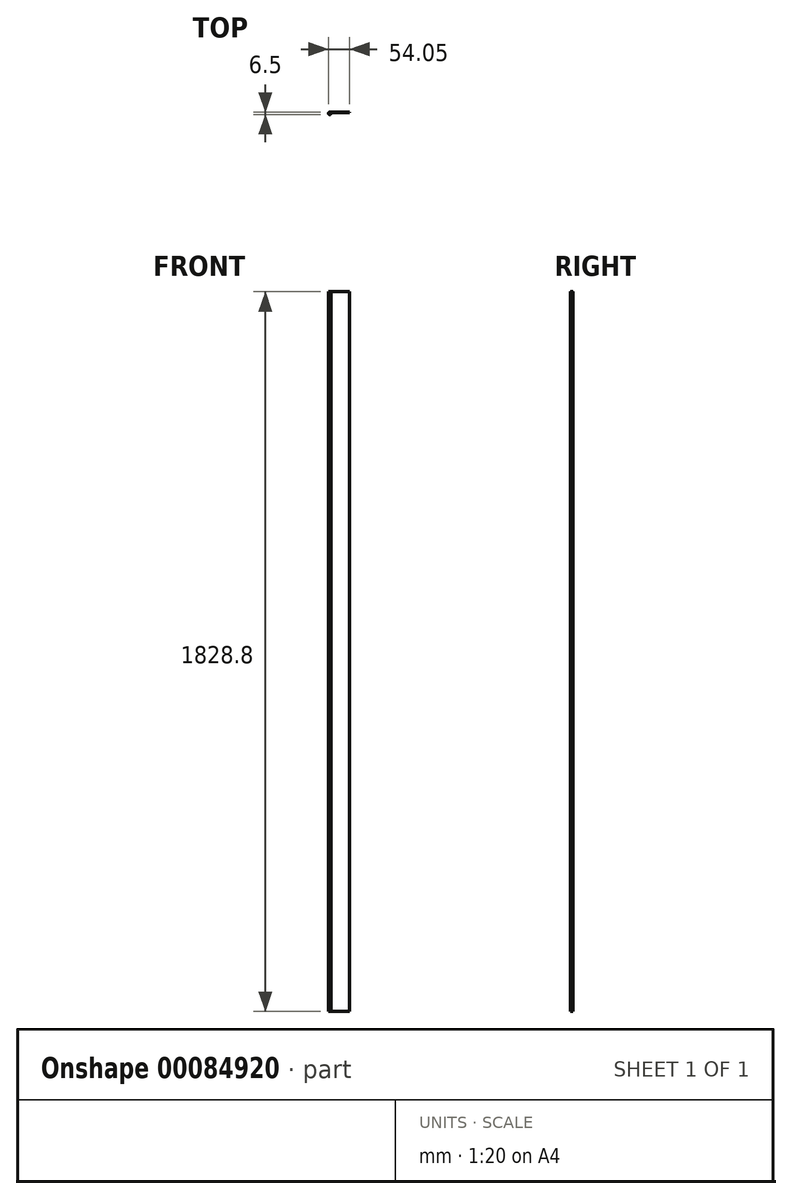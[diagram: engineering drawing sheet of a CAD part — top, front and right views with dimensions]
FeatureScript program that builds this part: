
annotation { "Feature Type Name" : "Feature", "Feature Type Description" : "" }
export const myFeature = defineFeature(function(context is Context, id is Id, definition is map)
    precondition{}
    {
        {
            var Q0;
            Q0=qCreatedBy(makeId("Top.planeOp"),FACE);
            var sketch = newSketch(context, id + "F0", { "sketchPlane" : qUnion([Q0])});
            skArc(sketch, "E0", {"start": v(0, 1.75) * mm, "mid": v(-0.85, -1.53) * mm, "end": v(1.5, 0.92) * mm});
            skArc(sketch, "E1", {"start": v(0, 3.25) * mm, "mid": v(-1.59, -2.84) * mm, "end": v(2.77, 1.7) * mm});
            skLineSegment(sketch, "E2.bottom", {"start": v(0, 3.25) * mm, "end": v(50.8, 3.25) * mm});
            skLineSegment(sketch, "E2.top", {"start": v(0, 1.75) * mm, "end": v(50.8, 1.75) * mm});
            skLineSegment(sketch, "E2.right", {"start": v(50.8, 3.25) * mm, "end": v(50.8, 1.75) * mm});
            skLineSegment(sketch, "E3", {"start": v(1.5, 0.92) * mm, "end": v(2.77, 1.7) * mm});
            skSolve(sketch);
        }
        {
            var Q0;
            Q0=makeQuery(id+"F0.imprint","IMPRINT",FACE,{"disambiguationData":[TD([[makeQuery(id+"F0.imprint","IMPRINT",EDGE,{"derivedFrom":sQuery(id+"F0.wireOp",EDGE,"E0")}),-1.0]])]});
            extrude(context, id + "F1", {"entities" : qUnion([Q0]), "depth" : 1828.8 * mm});
        }
        {
            var Q0;
            Q0=makeQuery(id+"F1.opExtrude","SWEPT_FACE",FACE,{"disambiguationData":[OSD([sQuery(id+"F0.wireOp",EDGE,"E2.top")])]});
            var sketch = newSketch(context, id + "F2", { "sketchPlane" : qUnion([Q0])});
            skSolve(sketch);
        }
    });
